FCSTD DOCUMENT  (FreeCAD 0.16R6710 (Git))
Label: front
License: All rights reserved
LicenseURL: http://en.wikipedia.org/wiki/All_rights_reserved
objects: Part::Part2DObjectPython×3, App::DocumentObjectGroup×1
note: 3 computed .brp shape members not serialized (recipe doc carries the construction recipe); baked Part::Feature solids carry a one-line shape summary decoded from their .brp

FEATURE [Part::Part2DObjectPython] Rectangle  label="front"  # Draft 2D object (typed FeaturePython)
  ChamferSize = 0
  Columns = 1
  FilletRadius = 0
  Height = 24
  Length = 79
  MakeFace = true
  Rows = 1
FEATURE [Part::Part2DObjectPython] Polygon  # Draft 2D object (typed FeaturePython)
  ChamferSize = 0
  DrawMode = 0
  FacesNumber = 6
  FilletRadius = 0
  MakeFace = true
  Placement = pos=(10.7839,11.9412,0) rot=(0,0,1;0rad)
  Radius = 10.7
FEATURE [Part::Part2DObjectPython] Rectangle001  label="indicator"  # Draft 2D object (typed FeaturePython)
  ChamferSize = 0
  Columns = 1
  FilletRadius = 0
  Height = 22.5
  Length = 14
  MakeFace = true
  Placement = pos=(27.443,5.46456,0) rot=(0.707107,0.707107,0;3.14159rad)
  Rows = 1
FEATURE [App::DocumentObjectGroup] Construction
  Group = -> [Rectangle,Polygon,Rectangle001]
